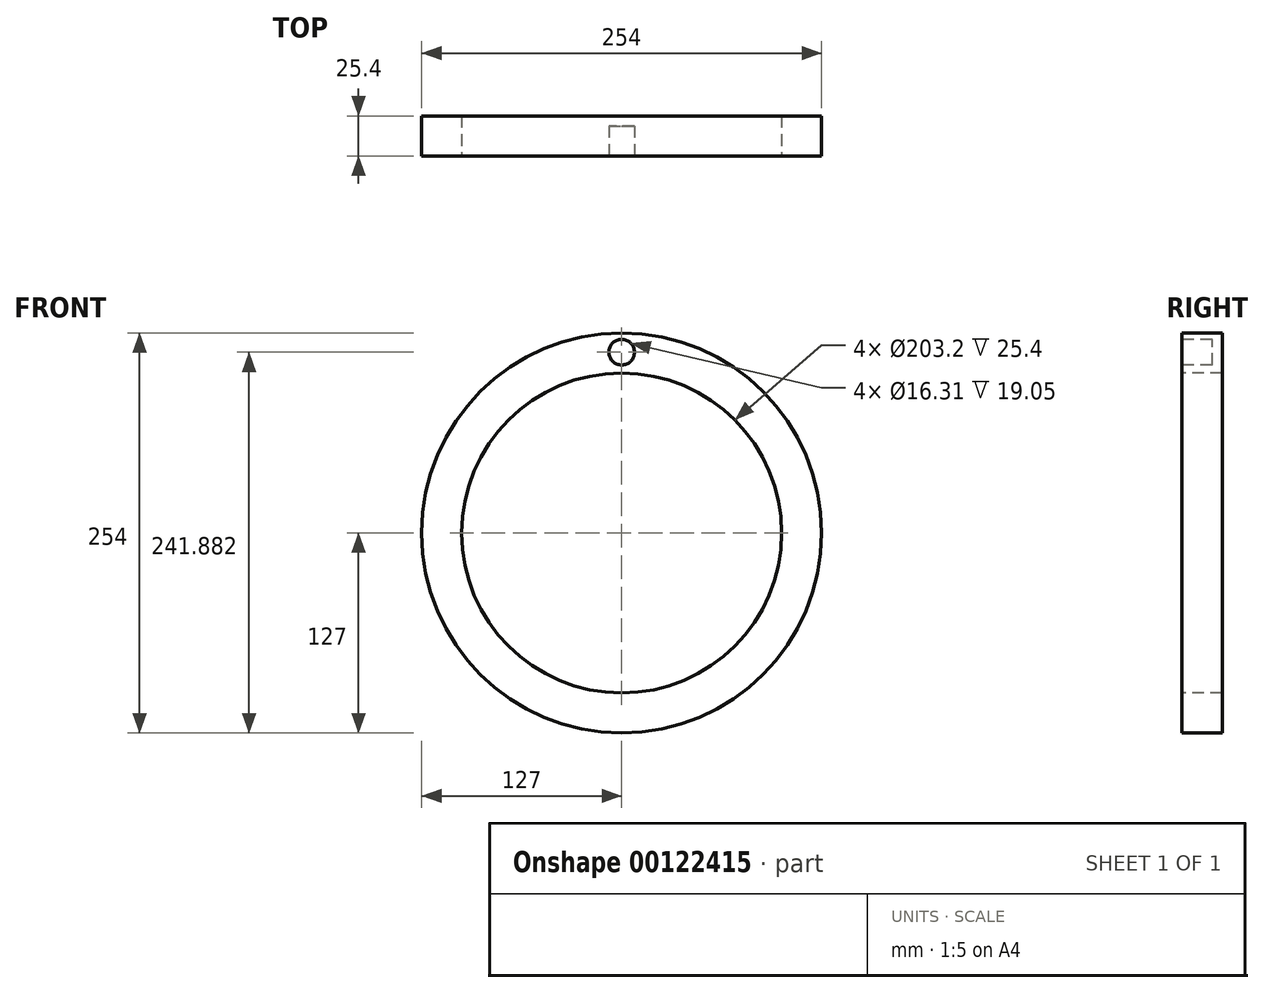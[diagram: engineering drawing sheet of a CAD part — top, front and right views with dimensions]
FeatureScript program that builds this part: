
annotation { "Feature Type Name" : "Feature", "Feature Type Description" : "" }
export const myFeature = defineFeature(function(context is Context, id is Id, definition is map)
    precondition{}
    {
        {
            var Q0;
            Q0=qCreatedBy(makeId("Front.planeOp"),FACE);
            var sketch = newSketch(context, id + "F0", { "sketchPlane" : qUnion([Q0])});
            skCircle(sketch, "E0", {"center": v(0, 0) * mm, "radius": 127 * mm});
            skSolve(sketch);
        }
        {
            var Q0;
            Q0 = qSketchRegion(id + "F0", true);
            extrude(context, id + "F1", {"entities" : qUnion([Q0]), "depth" : 25.4 * mm});
        }
        {
            var Q0;
            Q0=makeQuery(id+"F1.opExtrude","CAP_FACE",FACE,{"disambiguationData":[OSD([sQuery(id+"F0.wireOp",EDGE,"E0")])],"isStart":false});
            var sketch = newSketch(context, id + "F2", { "sketchPlane" : qUnion([Q0])});
            skCircle(sketch, "E1", {"center": v(0, 0) * mm, "radius": 101.6 * mm});
            skSolve(sketch);
        }
        {
            var Q0;
            Q0 = qSketchRegion(id + "F2", true);
            extrude(context, id + "F3", {"entities" : qUnion([Q0]), "operationType" : NewBodyOperationType.REMOVE, "endBound" : BoundingType.THROUGH_ALL, "oppositeDirection" : true, "depth" : 25.4 * mm});
        }
        {
            var Q0;
            Q0=makeQuery(id+"F1.opExtrude","CAP_FACE",FACE,{"disambiguationData":[OSD([sQuery(id+"F0.wireOp",EDGE,"E0")])],"isStart":false});
            var sketch = newSketch(context, id + "F4", { "sketchPlane" : qUnion([Q0])});
            skCircle(sketch, "E2", {"center": v(0, 0) * mm, "radius": 114.88 * mm});
            skCircle(sketch, "E3", {"center": v(0, 114.88) * mm, "radius": 8.16 * mm});
            skSolve(sketch);
        }
        {
            var Q0;
            {var subQ0=sQuery(id+"F4.wireOp",EDGE,"E2");var subQ1=sQuery(id+"F4.wireOp",EDGE,"E3");var subQ2=makeQuery(id+"F4.imprint","INTERSECT",VERTEX,{"disambiguationData":[OD(0.0)],"derivedFrom":[subQ1,subQ0]});Q0=makeQuery(id+"F4.imprint","IMPRINT",FACE,{"disambiguationData":[TD([[makeQuery(id+"F4.imprint","IMPRINT",EDGE,{"disambiguationData":[TD([[subQ2,-1.0]])],"derivedFrom":subQ1}),1.0]])]});}
            var Q1;
            {var subQ0=sQuery(id+"F4.wireOp",EDGE,"E2");var subQ1=sQuery(id+"F4.wireOp",EDGE,"E3");var subQ2=makeQuery(id+"F4.imprint","INTERSECT",VERTEX,{"disambiguationData":[OD(0.0)],"derivedFrom":[subQ1,subQ0]});Q1=makeQuery(id+"F4.imprint","IMPRINT",FACE,{"disambiguationData":[TD([[makeQuery(id+"F4.imprint","IMPRINT",EDGE,{"disambiguationData":[TD([[subQ2,1.0]])],"derivedFrom":subQ1}),1.0]])]});}
            extrude(context, id + "F5", {"entities" : qUnion([Q0, Q1]), "operationType" : NewBodyOperationType.REMOVE, "oppositeDirection" : true, "depth" : 19.05 * mm});
        }
    });
